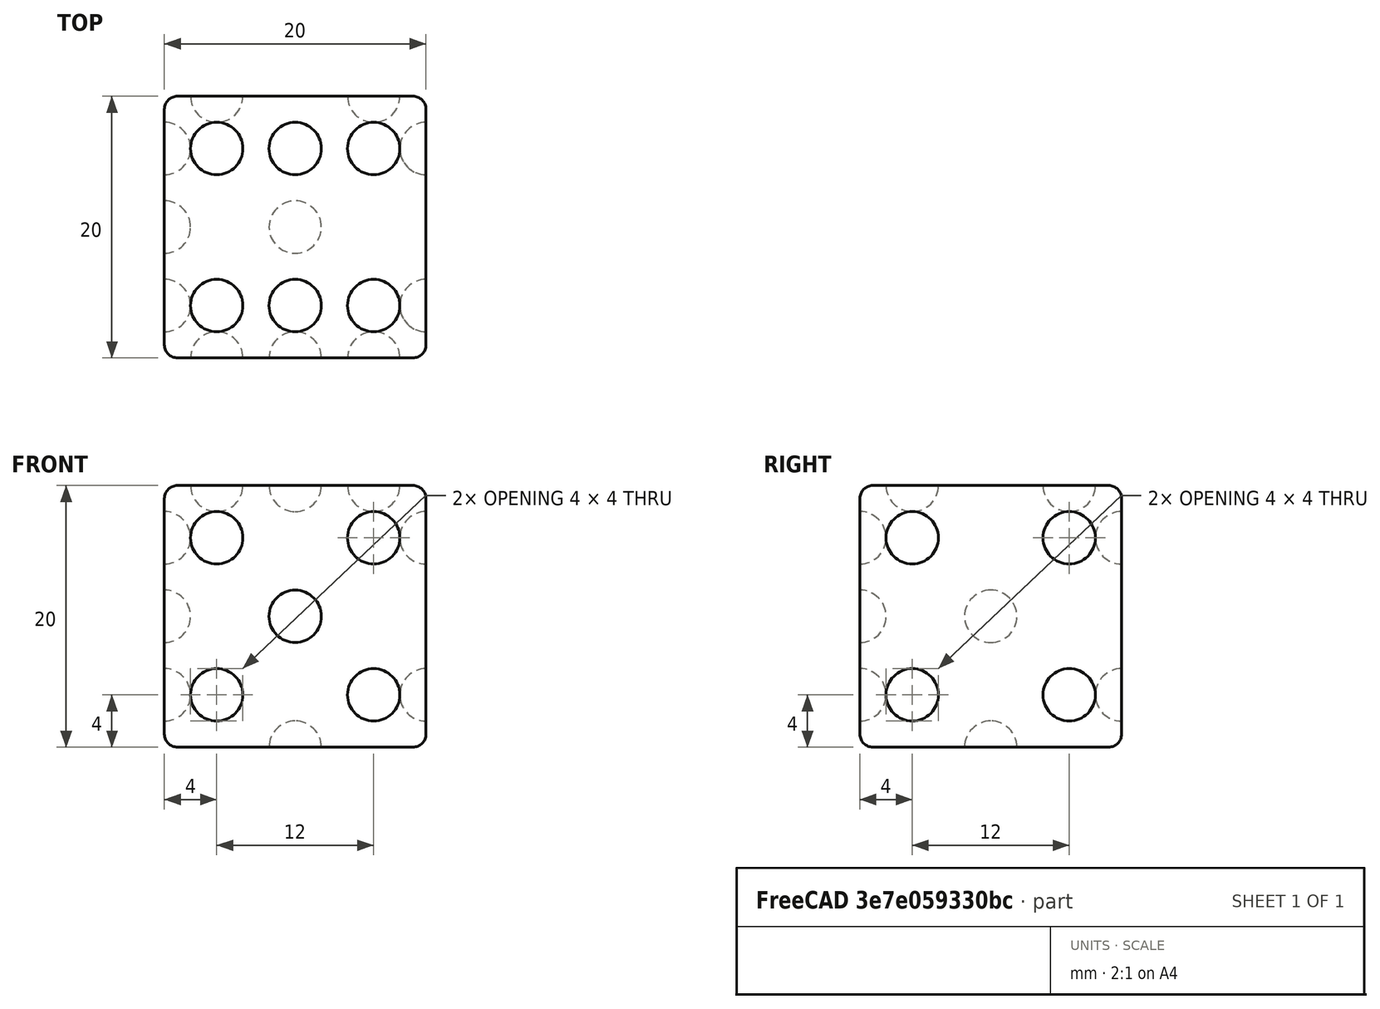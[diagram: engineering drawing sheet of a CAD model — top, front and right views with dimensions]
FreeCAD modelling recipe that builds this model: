
FCSTD DOCUMENT  (FreeCAD 0.21R33771 (Git))
Label: OJT1_T13R02_dau
License: All rights reserved
LicenseURL: http://en.wikipedia.org/wiki/All_rights_reserved
objects: Part::Sphere×21, Part::Cut×6, Part::MultiFuse×5, Part::Box×1, Part::Fillet×1
note: 34 computed .brp shape members not serialized (recipe doc carries the construction recipe); baked Part::Feature solids carry a one-line shape summary decoded from their .brp

FEATURE [Part::Box] Box  label="Cube"
  AttacherType = Attacher::AttachEngine3D
  Height = 20
  Length = 20
  Width = 20
FEATURE [Part::Sphere] Sphere  label="Sphere6"
  Angle1 = -90
  Angle2 = 90
  Angle3 = 360
  AttacherType = Attacher::AttachEngine3D
  Placement = pos=(4,4,20) rot=(0,0,1;0rad)
  Radius = 2
FEATURE [Part::Sphere] Sphere001
  Angle1 = -90
  Angle2 = 90
  Angle3 = 360
  AttacherType = Attacher::AttachEngine3D
  Placement = pos=(10,4,20) rot=(0,0,1;0rad)
  Radius = 2
FEATURE [Part::Sphere] Sphere002
  Angle1 = -90
  Angle2 = 90
  Angle3 = 360
  AttacherType = Attacher::AttachEngine3D
  Placement = pos=(16,4,20) rot=(0,0,1;0rad)
  Radius = 2
FEATURE [Part::Sphere] Sphere003
  Angle1 = -90
  Angle2 = 90
  Angle3 = 360
  AttacherType = Attacher::AttachEngine3D
  Placement = pos=(4,16,20) rot=(0,0,1;0rad)
  Radius = 2
FEATURE [Part::Sphere] Sphere005
  Angle1 = -90
  Angle2 = 90
  Angle3 = 360
  AttacherType = Attacher::AttachEngine3D
  Placement = pos=(10,16,20) rot=(0,0,1;0rad)
  Radius = 2
FEATURE [Part::Sphere] Sphere006
  Angle1 = -90
  Angle2 = 90
  Angle3 = 360
  AttacherType = Attacher::AttachEngine3D
  Placement = pos=(16,16,20) rot=(0,0,1;0rad)
  Radius = 2
FEATURE [Part::MultiFuse] Fusion
  Refine = true
  Shapes = -> [Sphere,Sphere001,Sphere002,Sphere003,Sphere005,Sphere006]
FEATURE [Part::Cut] Cut  label="num_6"
  Base = -> Box
  Refine = true
  Tool = -> Fusion
FEATURE [Part::Sphere] Sphere007  label="Sphere4"
  Angle1 = -90
  Angle2 = 90
  Angle3 = 360
  AttacherType = Attacher::AttachEngine3D
  Placement = pos=(20,4,16) rot=(0,0,1;0rad)
  Radius = 2
FEATURE [Part::Sphere] Sphere008
  Angle1 = -90
  Angle2 = 90
  Angle3 = 360
  AttacherType = Attacher::AttachEngine3D
  Placement = pos=(20,4,4) rot=(0,0,1;0rad)
  Radius = 2
FEATURE [Part::Sphere] Sphere009
  Angle1 = -90
  Angle2 = 90
  Angle3 = 360
  AttacherType = Attacher::AttachEngine3D
  Placement = pos=(20,16,16) rot=(0,0,1;0rad)
  Radius = 2
FEATURE [Part::Sphere] Sphere010
  Angle1 = -90
  Angle2 = 90
  Angle3 = 360
  AttacherType = Attacher::AttachEngine3D
  Placement = pos=(20,16,4) rot=(0,0,1;0rad)
  Radius = 2
FEATURE [Part::MultiFuse] Fusion001
  Refine = true
  Shapes = -> [Sphere007,Sphere008,Sphere009,Sphere010]
FEATURE [Part::Cut] Cut001  label="nums_6+4"
  Base = -> Cut
  Refine = true
  Tool = -> Fusion001
FEATURE [Part::Sphere] Sphere011  label="Sphere5"
  Angle1 = -90
  Angle2 = 90
  Angle3 = 360
  AttacherType = Attacher::AttachEngine3D
  Placement = pos=(4,0,4) rot=(0,0,1;0rad)
  Radius = 2
FEATURE [Part::Sphere] Sphere012
  Angle1 = -90
  Angle2 = 90
  Angle3 = 360
  AttacherType = Attacher::AttachEngine3D
  Placement = pos=(16,0,4) rot=(0,0,1;0rad)
  Radius = 2
FEATURE [Part::Sphere] Sphere013
  Angle1 = -90
  Angle2 = 90
  Angle3 = 360
  AttacherType = Attacher::AttachEngine3D
  Placement = pos=(4,0,16) rot=(0,0,1;0rad)
  Radius = 2
FEATURE [Part::Sphere] Sphere014
  Angle1 = -90
  Angle2 = 90
  Angle3 = 360
  AttacherType = Attacher::AttachEngine3D
  Placement = pos=(16,0,16) rot=(0,0,1;0rad)
  Radius = 2
FEATURE [Part::Sphere] Sphere015
  Angle1 = -90
  Angle2 = 90
  Angle3 = 360
  AttacherType = Attacher::AttachEngine3D
  Placement = pos=(10,0,10) rot=(0,0,1;0rad)
  Radius = 2
FEATURE [Part::MultiFuse] Fusion002
  Refine = true
  Shapes = -> [Sphere011,Sphere012,Sphere013,Sphere014,Sphere015]
FEATURE [Part::Cut] Cut002  label="nums_6+4+5"
  Base = -> Cut001
  Refine = true
  Tool = -> Fusion002
FEATURE [Part::Sphere] Sphere016  label="Sphere3"
  Angle1 = -90
  Angle2 = 90
  Angle3 = 360
  AttacherType = Attacher::AttachEngine3D
  Placement = pos=(0,4,4) rot=(0,0,1;0rad)
  Radius = 2
FEATURE [Part::Sphere] Sphere017
  Angle1 = -90
  Angle2 = 90
  Angle3 = 360
  AttacherType = Attacher::AttachEngine3D
  Placement = pos=(0,16,16) rot=(0,0,1;0rad)
  Radius = 2
FEATURE [Part::Sphere] Sphere018
  Angle1 = -90
  Angle2 = 90
  Angle3 = 360
  AttacherType = Attacher::AttachEngine3D
  Placement = pos=(0,10,10) rot=(0,0,1;0rad)
  Radius = 2
FEATURE [Part::MultiFuse] Fusion003
  Refine = true
  Shapes = -> [Sphere016,Sphere017,Sphere018]
FEATURE [Part::Cut] Cut003  label="nums_6+4+5+3"
  Base = -> Cut002
  Refine = true
  Tool = -> Fusion003
FEATURE [Part::Sphere] Sphere019  label="Sphere2"
  Angle1 = -90
  Angle2 = 90
  Angle3 = 360
  AttacherType = Attacher::AttachEngine3D
  Placement = pos=(4,20,4) rot=(0,0,1;0rad)
  Radius = 2
FEATURE [Part::Sphere] Sphere020
  Angle1 = -90
  Angle2 = 90
  Angle3 = 360
  AttacherType = Attacher::AttachEngine3D
  Placement = pos=(16,20,16) rot=(0,0,1;0rad)
  Radius = 2
FEATURE [Part::MultiFuse] Fusion004
  Refine = true
  Shapes = -> [Sphere019,Sphere020]
FEATURE [Part::Cut] Cut004  label="nums_6+5+4+3+2"
  Base = -> Cut003
  Refine = true
  Tool = -> Fusion004
FEATURE [Part::Sphere] Sphere021  label="Sphere1"
  Angle1 = -90
  Angle2 = 90
  Angle3 = 360
  AttacherType = Attacher::AttachEngine3D
  Placement = pos=(10,10,0) rot=(0,0,1;0rad)
  Radius = 2
FEATURE [Part::Cut] Cut005  label="nums_6+5+4+3+2+1"
  Base = -> Cut004
  Refine = true
  Tool = -> Sphere021
FEATURE [Part::Fillet] Fillet  label="dau"
  Base = -> Cut005
  Edges = 12 edges r=1: [Edge1,Edge2,Edge3,Edge4,Edge11,Edge12,Edge13,Edge24,Edge25,Edge32,Edge33,Edge35]
